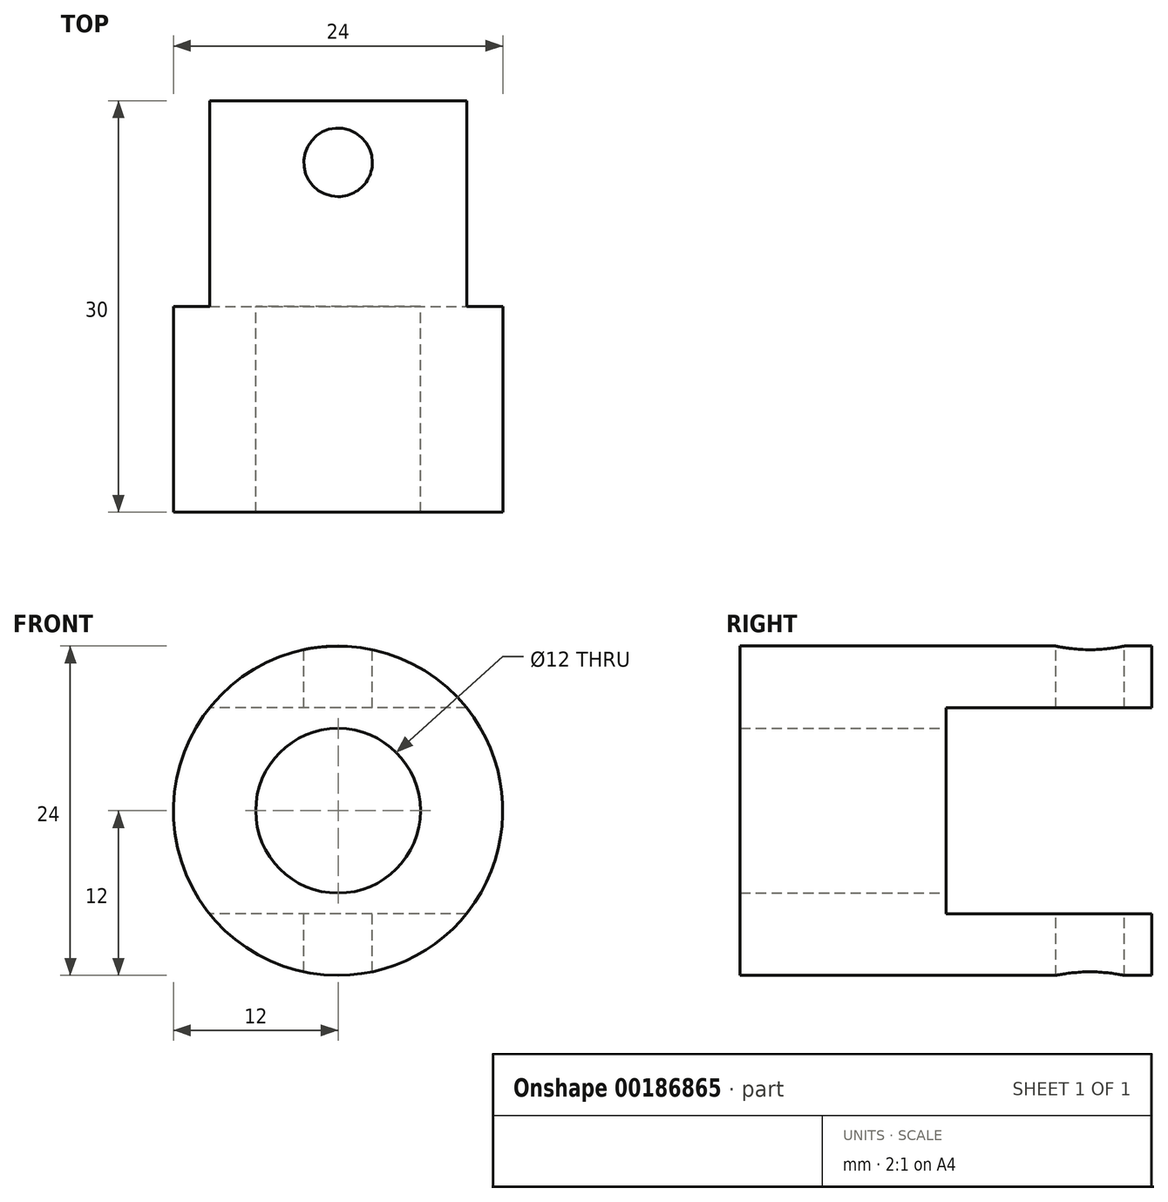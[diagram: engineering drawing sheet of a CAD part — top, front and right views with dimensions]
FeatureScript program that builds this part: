
annotation { "Feature Type Name" : "Feature", "Feature Type Description" : "" }
export const myFeature = defineFeature(function(context is Context, id is Id, definition is map)
    precondition{}
    {
        {
            var Q0;
            Q0=qCreatedBy(makeId("Front.planeOp"),FACE);
            var sketch = newSketch(context, id + "F0", { "sketchPlane" : qUnion([Q0])});
            skCircle(sketch, "E0", {"center": v(0, 0) * mm, "radius": 6 * mm});
            skCircle(sketch, "E1", {"center": v(0, 0) * mm, "radius": 12 * mm});
            skSolve(sketch);
        }
        {
            var Q0;
            Q0=makeQuery(id+"F0.imprint","IMPRINT",FACE,{"disambiguationData":[TD([[makeQuery(id+"F0.imprint","IMPRINT",EDGE,{"derivedFrom":sQuery(id+"F0.wireOp",EDGE,"E0")}),-1.0]])]});
            extrude(context, id + "F1", {"entities" : qUnion([Q0]), "depth" : 30 * mm});
        }
        {
            var Q0;
            Q0=qCreatedBy(makeId("Right.planeOp"),FACE);
            var sketch = newSketch(context, id + "F2", { "sketchPlane" : qUnion([Q0])});
            skLineSegment(sketch, "E2.bottom", {"start": v(15, 7.5) * mm, "end": v(-15, 7.5) * mm});
            skLineSegment(sketch, "E2.top", {"start": v(15, -7.5) * mm, "end": v(-15, -7.5) * mm});
            skLineSegment(sketch, "E2.left", {"start": v(15, 7.5) * mm, "end": v(15, -7.5) * mm});
            skLineSegment(sketch, "E2.right", {"start": v(-15, 7.5) * mm, "end": v(-15, -7.5) * mm});
            skPoint(sketch, "E2.middle", {"position": v(0, 0) * mm});
            skSolve(sketch);
        }
        {
            var Q0;
            Q0 = qSketchRegion(id + "F2", true);
            extrude(context, id + "F3", {"entities" : qUnion([Q0]), "operationType" : NewBodyOperationType.REMOVE, "endBound" : BoundingType.SYMMETRIC, "oppositeDirection" : true, "depth" : 25 * mm});
        }
        {
            var Q0;
            Q0=qCreatedBy(makeId("Top.planeOp"),FACE);
            var sketch = newSketch(context, id + "F4", { "sketchPlane" : qUnion([Q0])});
            skCircle(sketch, "E3", {"center": v(0, -4.5) * mm, "radius": 2.5 * mm});
            skSolve(sketch);
        }
        {
            var Q0;
            Q0 = qSketchRegion(id + "F4", true);
            extrude(context, id + "F5", {"entities" : qUnion([Q0]), "operationType" : NewBodyOperationType.REMOVE, "endBound" : BoundingType.SYMMETRIC, "oppositeDirection" : true, "depth" : 25 * mm});
        }
    });
